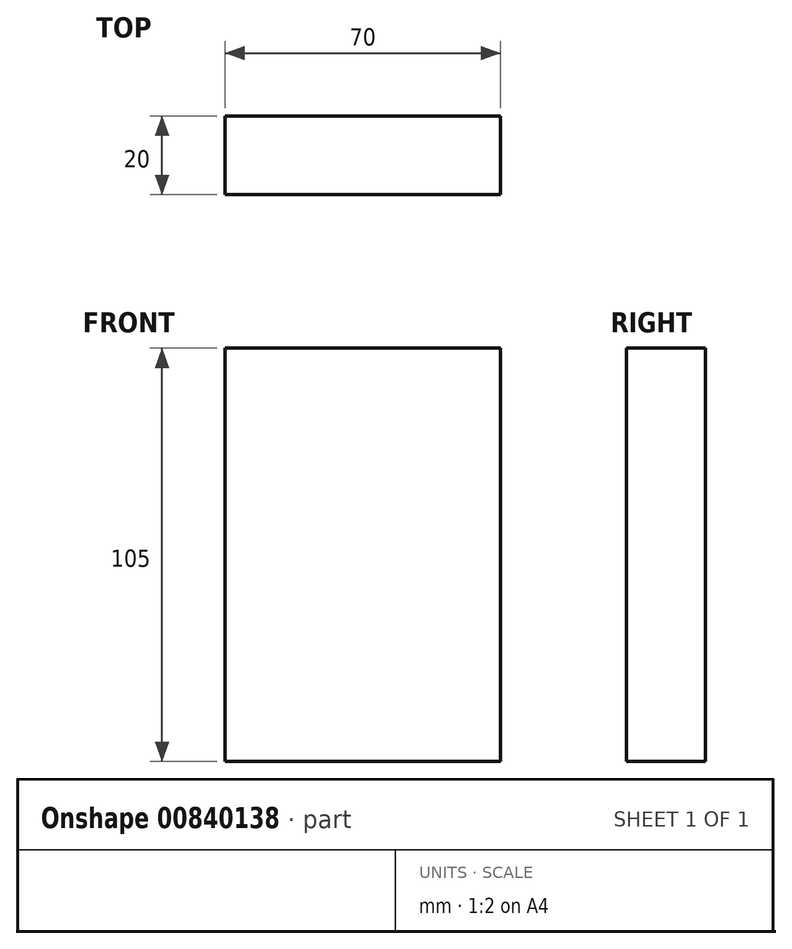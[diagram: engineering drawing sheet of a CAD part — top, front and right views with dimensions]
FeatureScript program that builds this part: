
annotation { "Feature Type Name" : "Feature", "Feature Type Description" : "" }
export const myFeature = defineFeature(function(context is Context, id is Id, definition is map)
    precondition{}
    {
        {
            var Q0;
            Q0=qCreatedBy(makeId("Front.planeOp"),FACE);
            var sketch = newSketch(context, id + "F0", { "sketchPlane" : qUnion([Q0])});
            skLineSegment(sketch, "E0.bottom", {"start": v(0, 0) * mm, "end": v(70, 0) * mm});
            skLineSegment(sketch, "E0.top", {"start": v(0, 105) * mm, "end": v(70, 105) * mm});
            skLineSegment(sketch, "E0.left", {"start": v(0, 0) * mm, "end": v(0, 105) * mm});
            skLineSegment(sketch, "E0.right", {"start": v(70, 0) * mm, "end": v(70, 105) * mm});
            skSolve(sketch);
        }
        {
            var Q0;
            Q0=makeQuery(id+"F0.imprint","IMPRINT",FACE,{"disambiguationData":[TD([[makeQuery(id+"F0.imprint","IMPRINT",EDGE,{"derivedFrom":sQuery(id+"F0.wireOp",EDGE,"E0.bottom")}),1.0]])]});
            extrude(context, id + "F1", {"entities" : qUnion([Q0]), "depth" : 20 * mm, "offsetDistance" : 25 * mm});
        }
    });
